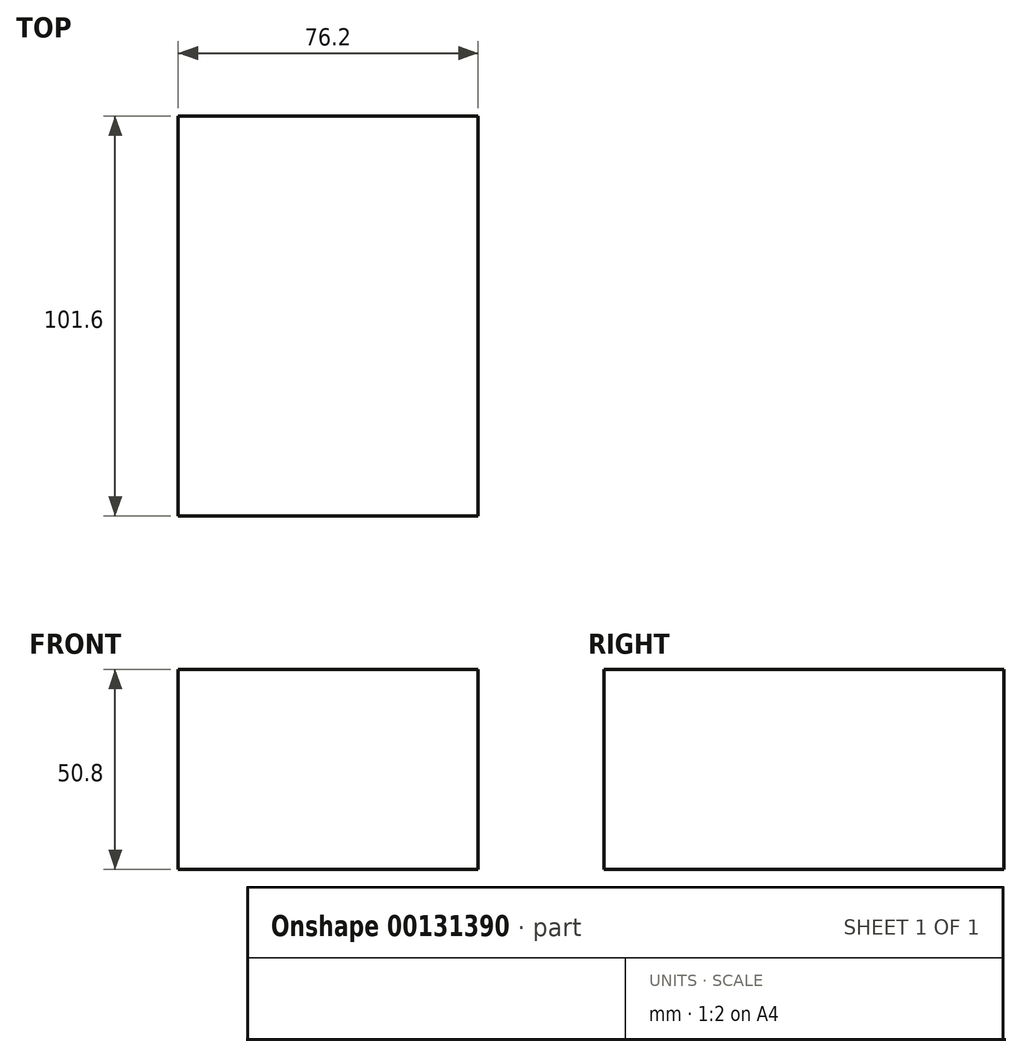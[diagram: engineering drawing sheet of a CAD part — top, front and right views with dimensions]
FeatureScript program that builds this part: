
annotation { "Feature Type Name" : "Feature", "Feature Type Description" : "" }
export const myFeature = defineFeature(function(context is Context, id is Id, definition is map)
    precondition{}
    {
        {
            var Q0;
            Q0=qCreatedBy(makeId("Front.planeOp"),FACE);
            var sketch = newSketch(context, id + "F0", { "sketchPlane" : qUnion([Q0])});
            skLineSegment(sketch, "E0.bottom", {"start": v(-38.1, 25.4) * mm, "end": v(38.1, 25.4) * mm});
            skLineSegment(sketch, "E0.top", {"start": v(-38.1, -25.4) * mm, "end": v(38.1, -25.4) * mm});
            skLineSegment(sketch, "E0.left", {"start": v(-38.1, 25.4) * mm, "end": v(-38.1, -25.4) * mm});
            skLineSegment(sketch, "E0.right", {"start": v(38.1, 25.4) * mm, "end": v(38.1, -25.4) * mm});
            skPoint(sketch, "E0.middle", {"position": v(0, 0) * mm});
            skSolve(sketch);
        }
        {
            var Q0;
            Q0=makeQuery(id+"F0.imprint","IMPRINT",FACE,{"disambiguationData":[TD([[makeQuery(id+"F0.imprint","IMPRINT",EDGE,{"derivedFrom":sQuery(id+"F0.wireOp",EDGE,"E0.bottom")}),-1.0]])]});
            extrude(context, id + "F1", {"entities" : qUnion([Q0]), "endBound" : BoundingType.SYMMETRIC, "depth" : 101.6 * mm});
        }
    });
